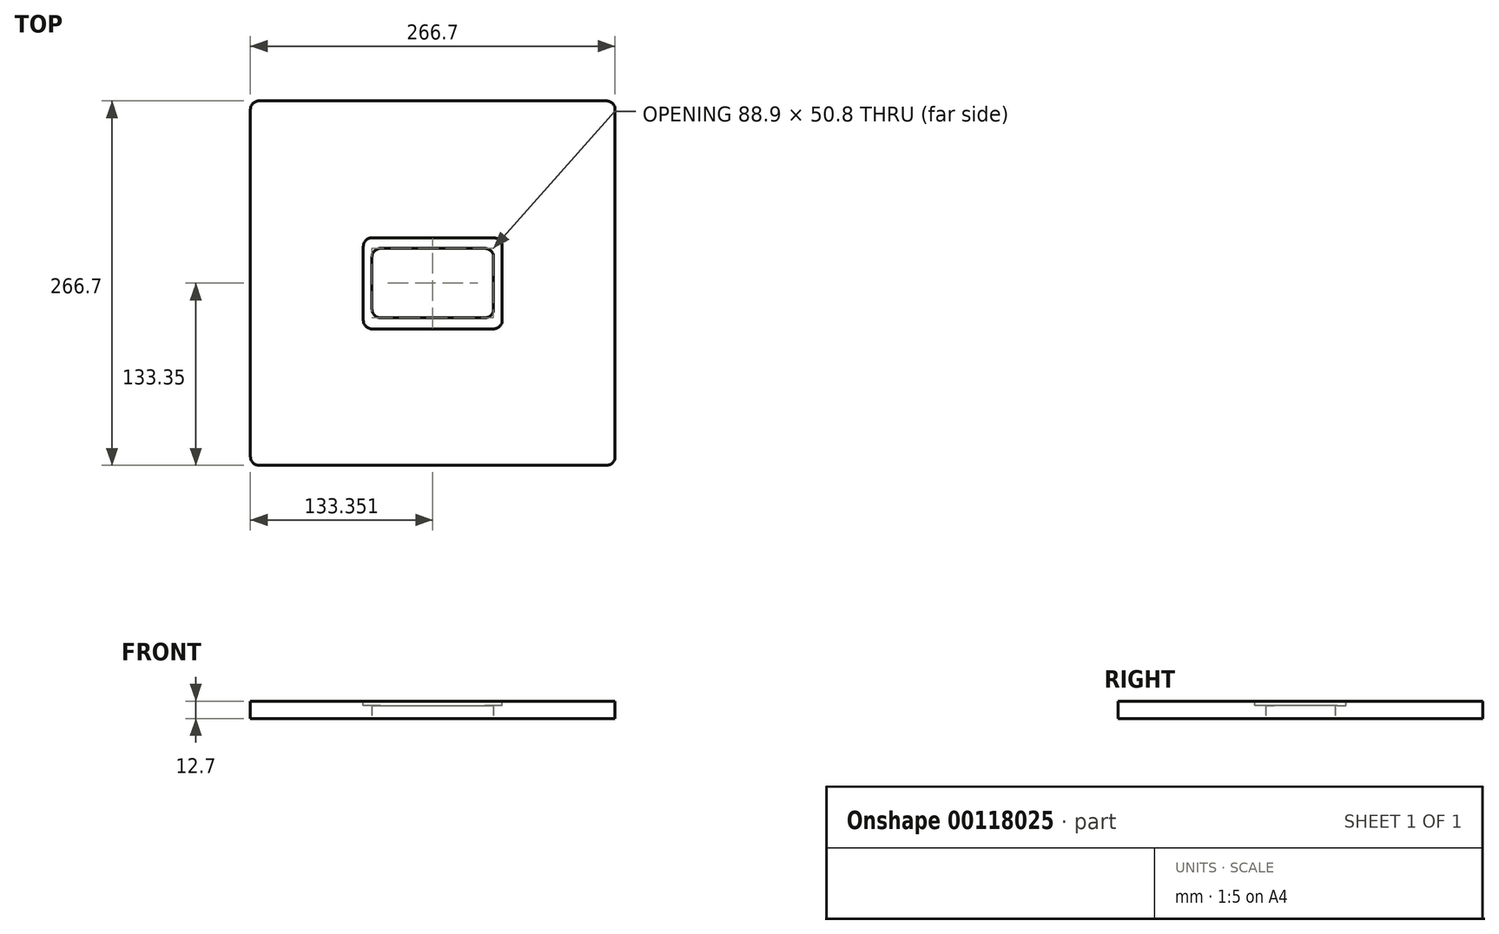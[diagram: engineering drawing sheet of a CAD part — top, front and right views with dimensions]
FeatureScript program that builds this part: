
annotation { "Feature Type Name" : "Feature", "Feature Type Description" : "" }
export const myFeature = defineFeature(function(context is Context, id is Id, definition is map)
    precondition{}
    {
        {
            var Q0;
            Q0=qCreatedBy(makeId("Top.planeOp"),FACE);
            var sketch = newSketch(context, id + "F0", { "sketchPlane" : qUnion([Q0])});
            skLineSegment(sketch, "E0.bottom", {"start": v(-40.24, 133.35) * mm, "end": v(213.76, 133.35) * mm});
            skLineSegment(sketch, "E0.top", {"start": v(-40.24, -133.35) * mm, "end": v(213.76, -133.35) * mm});
            skLineSegment(sketch, "E0.left", {"start": v(-46.59, 127) * mm, "end": v(-46.59, -127) * mm});
            skLineSegment(sketch, "E0.right", {"start": v(220.11, 127) * mm, "end": v(220.11, -127) * mm});
            skPoint(sketch, "E1.visualSharp", {"position": v(-46.59, 133.35) * mm});
            skArc(sketch, "E1.filletArc", {"start": v(-40.24, 133.35) * mm, "mid": v(-44.73, 131.5) * mm, "end": v(-46.59, 127) * mm});
            skPoint(sketch, "E2.visualSharp", {"position": v(220.11, 133.35) * mm});
            skArc(sketch, "E2.filletArc", {"start": v(220.11, 127) * mm, "mid": v(218.25, 131.5) * mm, "end": v(213.76, 133.35) * mm});
            skPoint(sketch, "E3.visualSharp", {"position": v(220.11, -133.35) * mm});
            skArc(sketch, "E3.filletArc", {"start": v(213.76, -133.35) * mm, "mid": v(218.25, -131.5) * mm, "end": v(220.11, -127) * mm});
            skPoint(sketch, "E4.visualSharp", {"position": v(-46.59, -133.35) * mm});
            skArc(sketch, "E4.filletArc", {"start": v(-46.59, -127) * mm, "mid": v(-44.73, -131.5) * mm, "end": v(-40.24, -133.35) * mm});
            skLineSegment(sketch, "E5.bottom", {"start": v(48.66, 25.4) * mm, "end": v(124.86, 25.4) * mm});
            skLineSegment(sketch, "E5.top", {"start": v(48.66, -25.4) * mm, "end": v(124.86, -25.4) * mm});
            skLineSegment(sketch, "E5.left", {"start": v(42.31, 19.05) * mm, "end": v(42.31, -19.05) * mm});
            skLineSegment(sketch, "E5.right", {"start": v(131.21, 19.05) * mm, "end": v(131.21, -19.05) * mm});
            skPoint(sketch, "E6.visualSharp", {"position": v(42.31, 25.4) * mm});
            skArc(sketch, "E6.filletArc", {"start": v(48.66, 25.4) * mm, "mid": v(44.17, 23.54) * mm, "end": v(42.31, 19.05) * mm});
            skPoint(sketch, "E7.visualSharp", {"position": v(131.21, 25.4) * mm});
            skArc(sketch, "E7.filletArc", {"start": v(131.21, 19.05) * mm, "mid": v(129.35, 23.54) * mm, "end": v(124.86, 25.4) * mm});
            skPoint(sketch, "E8.visualSharp", {"position": v(42.31, -25.4) * mm});
            skArc(sketch, "E8.filletArc", {"start": v(42.31, -19.05) * mm, "mid": v(44.17, -23.54) * mm, "end": v(48.66, -25.4) * mm});
            skPoint(sketch, "E9.visualSharp", {"position": v(131.21, -25.4) * mm});
            skArc(sketch, "E9.filletArc", {"start": v(124.86, -25.4) * mm, "mid": v(129.35, -23.54) * mm, "end": v(131.21, -19.05) * mm});
            skPoint(sketch, "E10", {"position": v(131.21, 0) * mm});
            skPoint(sketch, "E11", {"position": v(-46.59, 0) * mm});
            skLineSegment(sketch, "E12", {"start": v(124.86, 19.05) * mm, "end": v(48.66, -19.05) * mm, "construction": true});
            skLineSegment(sketch, "E13", {"start": v(48.66, 19.05) * mm, "end": v(124.86, -19.05) * mm, "construction": true});
            skLineSegment(sketch, "E14", {"start": v(86.76, 0) * mm, "end": v(86.76, 78.75) * mm, "construction": true});
            skPoint(sketch, "E15", {"position": v(86.76, 133.35) * mm});
            skSolve(sketch);
        }
        {
            var Q0;
            Q0 = qSketchRegion(id + "F0", true);
            extrude(context, id + "F1", {"entities" : qUnion([Q0]), "depth" : 12.7 * mm});
        }
        {
            var Q0;
            Q0=makeQuery(id+"F1.opExtrude","CAP_FACE",FACE,{"disambiguationData":[OSD([sQuery(id+"F0.wireOp",EDGE,"E0.bottom"),sQuery(id+"F0.wireOp",EDGE,"E0.top"),sQuery(id+"F0.wireOp",EDGE,"E0.left"),sQuery(id+"F0.wireOp",EDGE,"E0.right"),sQuery(id+"F0.wireOp",EDGE,"E1.filletArc"),sQuery(id+"F0.wireOp",EDGE,"E2.filletArc"),sQuery(id+"F0.wireOp",EDGE,"E3.filletArc"),sQuery(id+"F0.wireOp",EDGE,"E4.filletArc"),sQuery(id+"F0.wireOp",EDGE,"E5.bottom"),sQuery(id+"F0.wireOp",EDGE,"E5.top"),sQuery(id+"F0.wireOp",EDGE,"E5.left"),sQuery(id+"F0.wireOp",EDGE,"E5.right"),sQuery(id+"F0.wireOp",EDGE,"E6.filletArc"),sQuery(id+"F0.wireOp",EDGE,"E7.filletArc"),sQuery(id+"F0.wireOp",EDGE,"E8.filletArc"),sQuery(id+"F0.wireOp",EDGE,"E9.filletArc")])],"isStart":false});
            var sketch = newSketch(context, id + "F2", { "sketchPlane" : qUnion([Q0])});
            skLineSegment(sketch, "E16.bottom", {"start": v(42.3, 33.18) * mm, "end": v(131.2, 33.18) * mm});
            skLineSegment(sketch, "E16.top", {"start": v(42.3, -33.5) * mm, "end": v(131.2, -33.5) * mm});
            skLineSegment(sketch, "E16.left", {"start": v(35.96, 26.83) * mm, "end": v(35.96, -27.15) * mm});
            skLineSegment(sketch, "E16.right", {"start": v(137.56, 26.83) * mm, "end": v(137.56, -27.15) * mm});
            skPoint(sketch, "E17.visualSharp", {"position": v(35.96, 33.18) * mm});
            skArc(sketch, "E17.filletArc", {"start": v(42.3, 33.18) * mm, "mid": v(37.82, 31.32) * mm, "end": v(35.96, 26.83) * mm});
            skPoint(sketch, "E18.visualSharp", {"position": v(137.56, 33.18) * mm});
            skArc(sketch, "E18.filletArc", {"start": v(137.56, 26.83) * mm, "mid": v(135.7, 31.32) * mm, "end": v(131.2, 33.18) * mm});
            skPoint(sketch, "E19.visualSharp", {"position": v(137.56, -33.5) * mm});
            skArc(sketch, "E19.filletArc", {"start": v(131.2, -33.5) * mm, "mid": v(135.7, -31.64) * mm, "end": v(137.56, -27.15) * mm});
            skPoint(sketch, "E20.visualSharp", {"position": v(35.96, -33.5) * mm});
            skArc(sketch, "E20.filletArc", {"start": v(35.96, -27.15) * mm, "mid": v(37.82, -31.64) * mm, "end": v(42.3, -33.5) * mm});
            skSolve(sketch);
        }
        {
            var Q0;
            Q0=makeQuery(id+"F2.imprint","IMPRINT",FACE,{"disambiguationData":[TD([[makeQuery(id+"F2.imprint","IMPRINT",EDGE,{"derivedFrom":sQuery(id+"F2.wireOp",EDGE,"E16.bottom")}),-1.0]])]});
            extrude(context, id + "F3", {"entities" : qUnion([Q0]), "operationType" : NewBodyOperationType.REMOVE, "oppositeDirection" : true, "depth" : 3.17 * mm});
        }
    });
